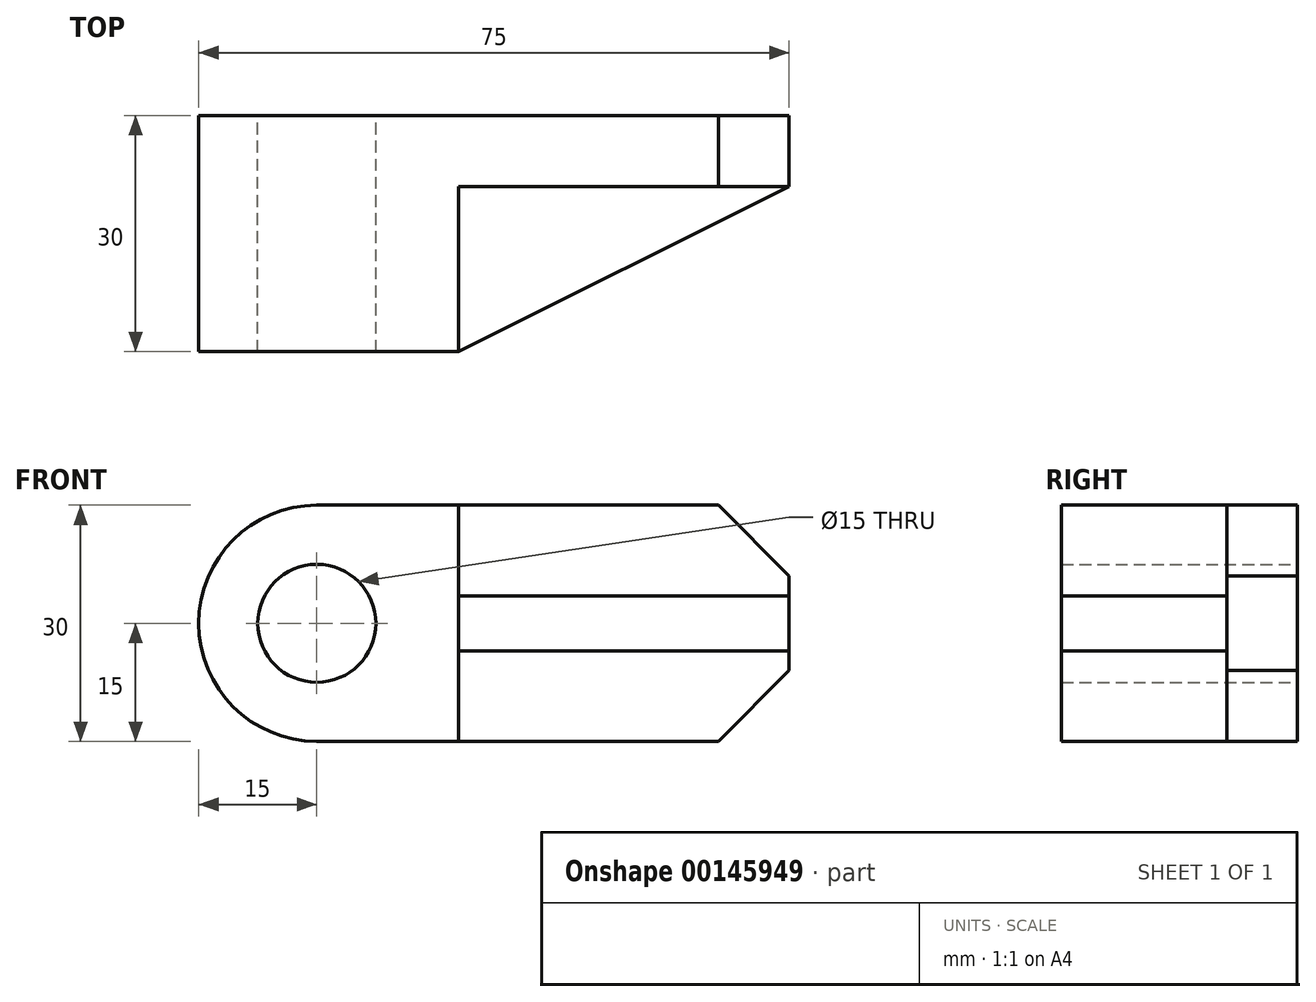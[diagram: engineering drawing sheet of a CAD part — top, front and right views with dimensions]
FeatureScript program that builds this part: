
annotation { "Feature Type Name" : "Feature", "Feature Type Description" : "" }
export const myFeature = defineFeature(function(context is Context, id is Id, definition is map)
    precondition{}
    {
        {
            var Q0;
            Q0=qCreatedBy(makeId("Front.planeOp"),FACE);
            var sketch = newSketch(context, id + "F0", { "sketchPlane" : qUnion([Q0])});
            skArc(sketch, "E0", {"start": v(0, 15) * mm, "mid": v(-15, 0) * mm, "end": v(0, -15) * mm});
            skCircle(sketch, "E1", {"center": v(0, 0) * mm, "radius": 7.5 * mm});
            skLineSegment(sketch, "E2", {"start": v(0, 15) * mm, "end": v(18, 15) * mm});
            skLineSegment(sketch, "E3", {"start": v(0, -15) * mm, "end": v(18, -15) * mm});
            skLineSegment(sketch, "E4", {"start": v(18, 15) * mm, "end": v(18, -15) * mm});
            skLineSegment(sketch, "E5", {"start": v(18, 15) * mm, "end": v(51, 15) * mm});
            skLineSegment(sketch, "E6", {"start": v(51, 15) * mm, "end": v(60, 6) * mm});
            skLineSegment(sketch, "E7", {"start": v(60, 6) * mm, "end": v(60, -6) * mm});
            skLineSegment(sketch, "E8", {"start": v(60, -6) * mm, "end": v(51, -15) * mm});
            skLineSegment(sketch, "E9", {"start": v(51, -15) * mm, "end": v(18, -15) * mm});
            skSolve(sketch);
        }
        {
            var Q0;
            Q0=makeQuery(id+"F0.imprint","IMPRINT",FACE,{"disambiguationData":[TD([[makeQuery(id+"F0.imprint","IMPRINT",EDGE,{"derivedFrom":sQuery(id+"F0.wireOp",EDGE,"E0")}),1.0]])]});
            extrude(context, id + "F1", {"entities" : qUnion([Q0]), "depth" : 30 * mm});
        }
        {
            var Q0;
            Q0=makeQuery(id+"F0.imprint","IMPRINT",FACE,{"disambiguationData":[TD([[makeQuery(id+"F0.imprint","IMPRINT",EDGE,{"derivedFrom":sQuery(id+"F0.wireOp",EDGE,"E4")}),1.0]])]});
            extrude(context, id + "F2", {"entities" : qUnion([Q0]), "operationType" : NewBodyOperationType.ADD, "depth" : 9 * mm});
        }
        {
            var Q0;
            Q0=qCreatedBy(makeId("Top.planeOp"),FACE);
            var sketch = newSketch(context, id + "F3", { "sketchPlane" : qUnion([Q0])});
            skLineSegment(sketch, "E10.0", {"start": v(0, -30) * mm, "end": v(18, -30) * mm, "construction": true});
            skLineSegment(sketch, "E11.0", {"start": v(60, -9) * mm, "end": v(51, -9) * mm, "construction": true});
            skLineSegment(sketch, "E12", {"start": v(18, -30) * mm, "end": v(60, -9) * mm});
            skLineSegment(sketch, "E13", {"start": v(60, -9) * mm, "end": v(18, -9) * mm});
            skLineSegment(sketch, "E14", {"start": v(18, -9) * mm, "end": v(18, -30) * mm});
            skSolve(sketch);
        }
        {
            var Q0;
            Q0 = qSketchRegion(id + "F3", true);
            extrude(context, id + "F4", {"entities" : qUnion([Q0]), "operationType" : NewBodyOperationType.ADD, "endBound" : BoundingType.SYMMETRIC, "depth" : 7 * mm});
        }
    });
